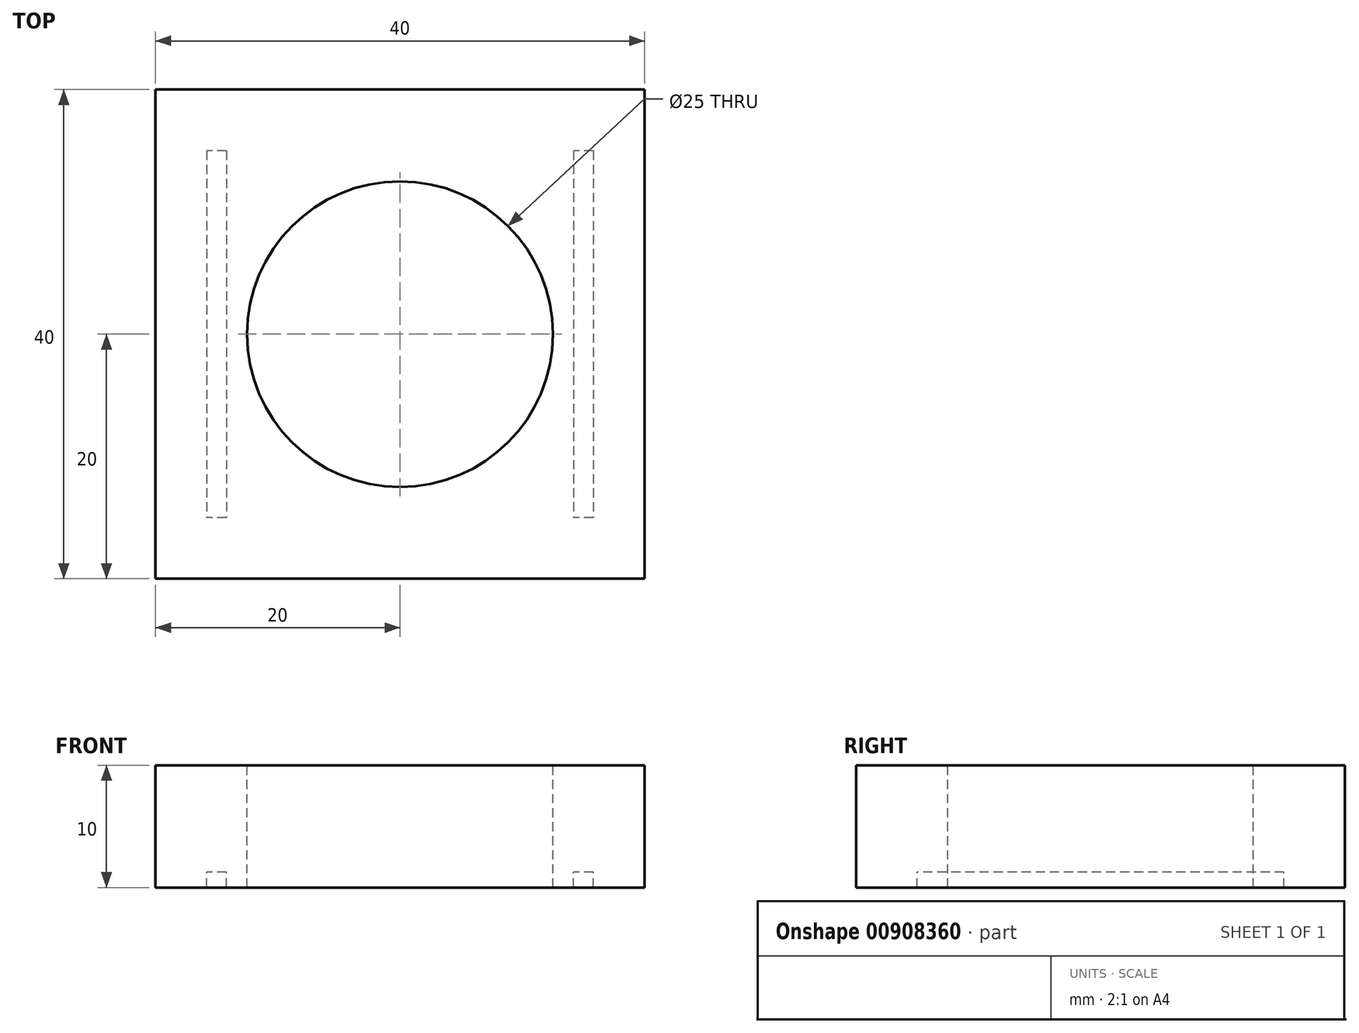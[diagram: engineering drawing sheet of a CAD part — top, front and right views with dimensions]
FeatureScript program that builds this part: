
annotation { "Feature Type Name" : "Feature", "Feature Type Description" : "" }
export const myFeature = defineFeature(function(context is Context, id is Id, definition is map)
    precondition{}
    {
        {
            var Q0;
            Q0=qCreatedBy(makeId("Top.planeOp"),FACE);
            var sketch = newSketch(context, id + "F0", { "sketchPlane" : qUnion([Q0])});
            skLineSegment(sketch, "E0.bottom", {"start": v(20, -20) * mm, "end": v(-20, -20) * mm});
            skLineSegment(sketch, "E0.top", {"start": v(20, 20) * mm, "end": v(-20, 20) * mm});
            skLineSegment(sketch, "E0.left", {"start": v(20, -20) * mm, "end": v(20, 20) * mm});
            skLineSegment(sketch, "E0.right", {"start": v(-20, -20) * mm, "end": v(-20, 20) * mm});
            skPoint(sketch, "E0.middle", {"position": v(0, 0) * mm});
            skSolve(sketch);
        }
        {
            var Q0;
            Q0=makeQuery(id+"F0.imprint","IMPRINT",FACE,{"disambiguationData":[TD([[makeQuery(id+"F0.imprint","IMPRINT",EDGE,{"derivedFrom":sQuery(id+"F0.wireOp",EDGE,"E0.bottom")}),-1.0]])]});
            extrude(context, id + "F1", {"entities" : qUnion([Q0]), "depth" : 10 * mm, "offsetDistance" : 25 * mm});
        }
        {
            var Q0;
            Q0=qCreatedBy(makeId("Top.planeOp"),FACE);
            var sketch = newSketch(context, id + "F2", { "sketchPlane" : qUnion([Q0])});
            skLineSegment(sketch, "E1.bottom", {"start": v(-14.2, 15) * mm, "end": v(-15.8, 15) * mm});
            skLineSegment(sketch, "E1.top", {"start": v(-14.2, -15) * mm, "end": v(-15.8, -15) * mm});
            skLineSegment(sketch, "E1.left", {"start": v(-14.2, 15) * mm, "end": v(-14.2, -15) * mm});
            skLineSegment(sketch, "E1.right", {"start": v(-15.8, 15) * mm, "end": v(-15.8, -15) * mm});
            skPoint(sketch, "E1.middle", {"position": v(-15, 0) * mm});
            skLineSegment(sketch, "E2.bottom", {"start": v(15.8, 15) * mm, "end": v(14.2, 15) * mm});
            skLineSegment(sketch, "E2.top", {"start": v(15.8, -15) * mm, "end": v(14.2, -15) * mm});
            skLineSegment(sketch, "E2.left", {"start": v(15.8, 15) * mm, "end": v(15.8, -15) * mm});
            skLineSegment(sketch, "E2.right", {"start": v(14.2, 15) * mm, "end": v(14.2, -15) * mm});
            skPoint(sketch, "E2.middle", {"position": v(15, 0) * mm});
            skSolve(sketch);
        }
        {
            var Q0;
            Q0=makeQuery(id+"F2.imprint","IMPRINT",FACE,{"disambiguationData":[TD([[makeQuery(id+"F2.imprint","IMPRINT",EDGE,{"derivedFrom":sQuery(id+"F2.wireOp",EDGE,"E1.bottom")}),1.0]])]});
            var Q1;
            Q1 = qSketchRegion(id + "F2", true);
            extrude(context, id + "F3", {"entities" : qUnion([Q0, Q1]), "operationType" : NewBodyOperationType.REMOVE, "endBound" : BoundingType.SYMMETRIC, "oppositeDirection" : true, "depth" : 2.5 * mm, "offsetDistance" : 25 * mm});
        }
        {
            var Q0;
            Q0=qCreatedBy(makeId("Top.planeOp"),FACE);
            var sketch = newSketch(context, id + "F4", { "sketchPlane" : qUnion([Q0])});
            skCircle(sketch, "E3", {"center": v(0, 0) * mm, "radius": 12.5 * mm});
            skSolve(sketch);
        }
        {
            var Q0;
            Q0 = qSketchRegion(id + "F4", true);
            extrude(context, id + "F5", {"entities" : qUnion([Q0]), "operationType" : NewBodyOperationType.REMOVE, "endBound" : BoundingType.SYMMETRIC, "oppositeDirection" : true, "depth" : 25 * mm, "offsetDistance" : 25 * mm});
        }
    });
